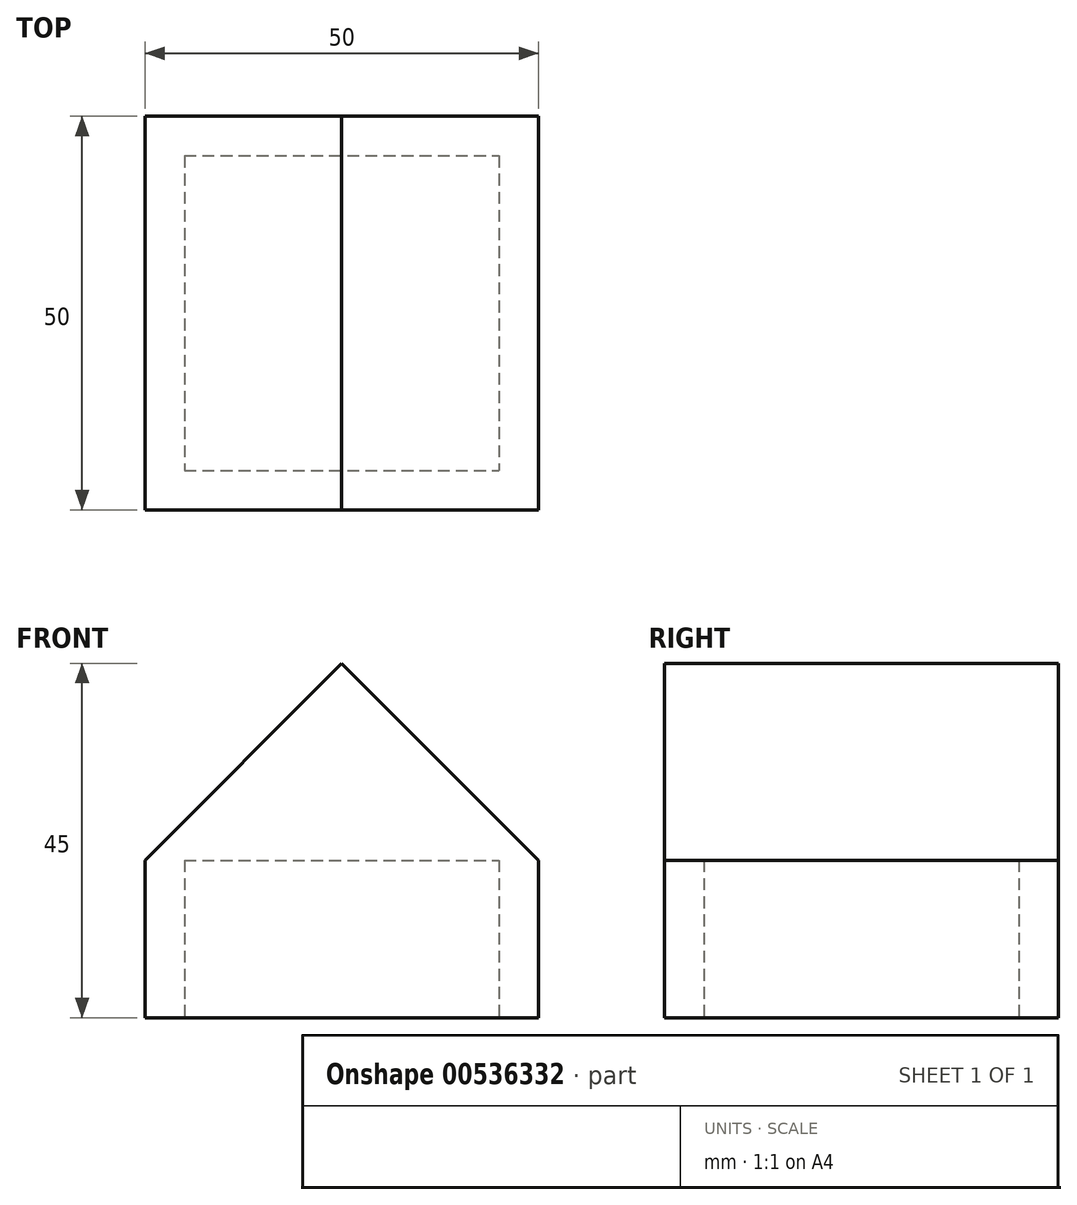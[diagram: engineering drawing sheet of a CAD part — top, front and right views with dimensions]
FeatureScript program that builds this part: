
annotation { "Feature Type Name" : "Feature", "Feature Type Description" : "" }
export const myFeature = defineFeature(function(context is Context, id is Id, definition is map)
    precondition{}
    {
        {
            var Q0;
            Q0=qCreatedBy(makeId("Top.planeOp"),FACE);
            var sketch = newSketch(context, id + "F0", { "sketchPlane" : qUnion([Q0])});
            skLineSegment(sketch, "E0.bottom", {"start": v(0, 0) * mm, "end": v(50, 0) * mm});
            skLineSegment(sketch, "E0.top", {"start": v(0, 50) * mm, "end": v(50, 50) * mm});
            skLineSegment(sketch, "E0.left", {"start": v(0, 0) * mm, "end": v(0, 50) * mm});
            skLineSegment(sketch, "E0.right", {"start": v(50, 0) * mm, "end": v(50, 50) * mm});
            skLineSegment(sketch, "E1", {"start": v(0, 25) * mm, "end": v(50.95, 25) * mm, "construction": true});
            skPoint(sketch, "E1.endSnap0", {"position": v(50, 25) * mm});
            skLineSegment(sketch, "E2", {"start": v(25, 50) * mm, "end": v(25, 0) * mm, "construction": true});
            skLineSegment(sketch, "E3.bottom", {"start": v(5, 45) * mm, "end": v(45, 45) * mm});
            skLineSegment(sketch, "E3.top", {"start": v(5, 5) * mm, "end": v(45, 5) * mm});
            skLineSegment(sketch, "E3.left", {"start": v(5, 45) * mm, "end": v(5, 5) * mm});
            skLineSegment(sketch, "E3.right", {"start": v(45, 45) * mm, "end": v(45, 5) * mm});
            skPoint(sketch, "E3.middle", {"position": v(25, 25) * mm});
            skSolve(sketch);
        }
        {
            var Q0;
            Q0 = qSketchRegion(id + "F0", true);
            extrude(context, id + "F1", {"entities" : qUnion([Q0]), "depth" : 20 * mm, "offsetDistance" : 25 * mm});
        }
        {
            var Q0;
            Q0=makeQuery(id+"F1.opExtrude","CAP_FACE",FACE,{"disambiguationData":[OSD([sQuery(id+"F0.wireOp",EDGE,"E0.bottom"),sQuery(id+"F0.wireOp",EDGE,"E0.top"),sQuery(id+"F0.wireOp",EDGE,"E0.left"),sQuery(id+"F0.wireOp",EDGE,"E0.right"),sQuery(id+"F0.wireOp",EDGE,"E3.bottom"),sQuery(id+"F0.wireOp",EDGE,"E3.top"),sQuery(id+"F0.wireOp",EDGE,"E3.left"),sQuery(id+"F0.wireOp",EDGE,"E3.right")])],"isStart":false});
            var sketch = newSketch(context, id + "F2", { "sketchPlane" : qUnion([Q0])});
            skLineSegment(sketch, "E4.bottom", {"start": v(0, 50) * mm, "end": v(50, 50) * mm});
            skLineSegment(sketch, "E4.top", {"start": v(0, 0) * mm, "end": v(50, 0) * mm});
            skLineSegment(sketch, "E4.left", {"start": v(0, 50) * mm, "end": v(0, 0) * mm});
            skLineSegment(sketch, "E4.right", {"start": v(50, 50) * mm, "end": v(50, 0) * mm});
            skSolve(sketch);
        }
        {
            var Q0;
            Q0 = qSketchRegion(id + "F2", true);
            extrude(context, id + "F3", {"entities" : qUnion([Q0]), "operationType" : NewBodyOperationType.ADD, "depth" : 25 * mm, "offsetDistance" : 25 * mm});
        }
        {
            var Q0;
            Q0=makeQuery(id+"F3.opExtrude","CAP_EDGE",EDGE,{"disambiguationData":[OSD([sQuery(id+"F2.wireOp",EDGE,"E4.left")])],"isStart":false});
            var Q1;
            Q1=makeQuery(id+"F3.opExtrude","CAP_EDGE",EDGE,{"disambiguationData":[OSD([sQuery(id+"F2.wireOp",EDGE,"E4.right")])],"isStart":false});
            chamfer(context, id + "F4", {"entities" : qUnion([Q0, Q1]), "width" : 25 * mm, "tangentPropagation" : true});
        }
    });
